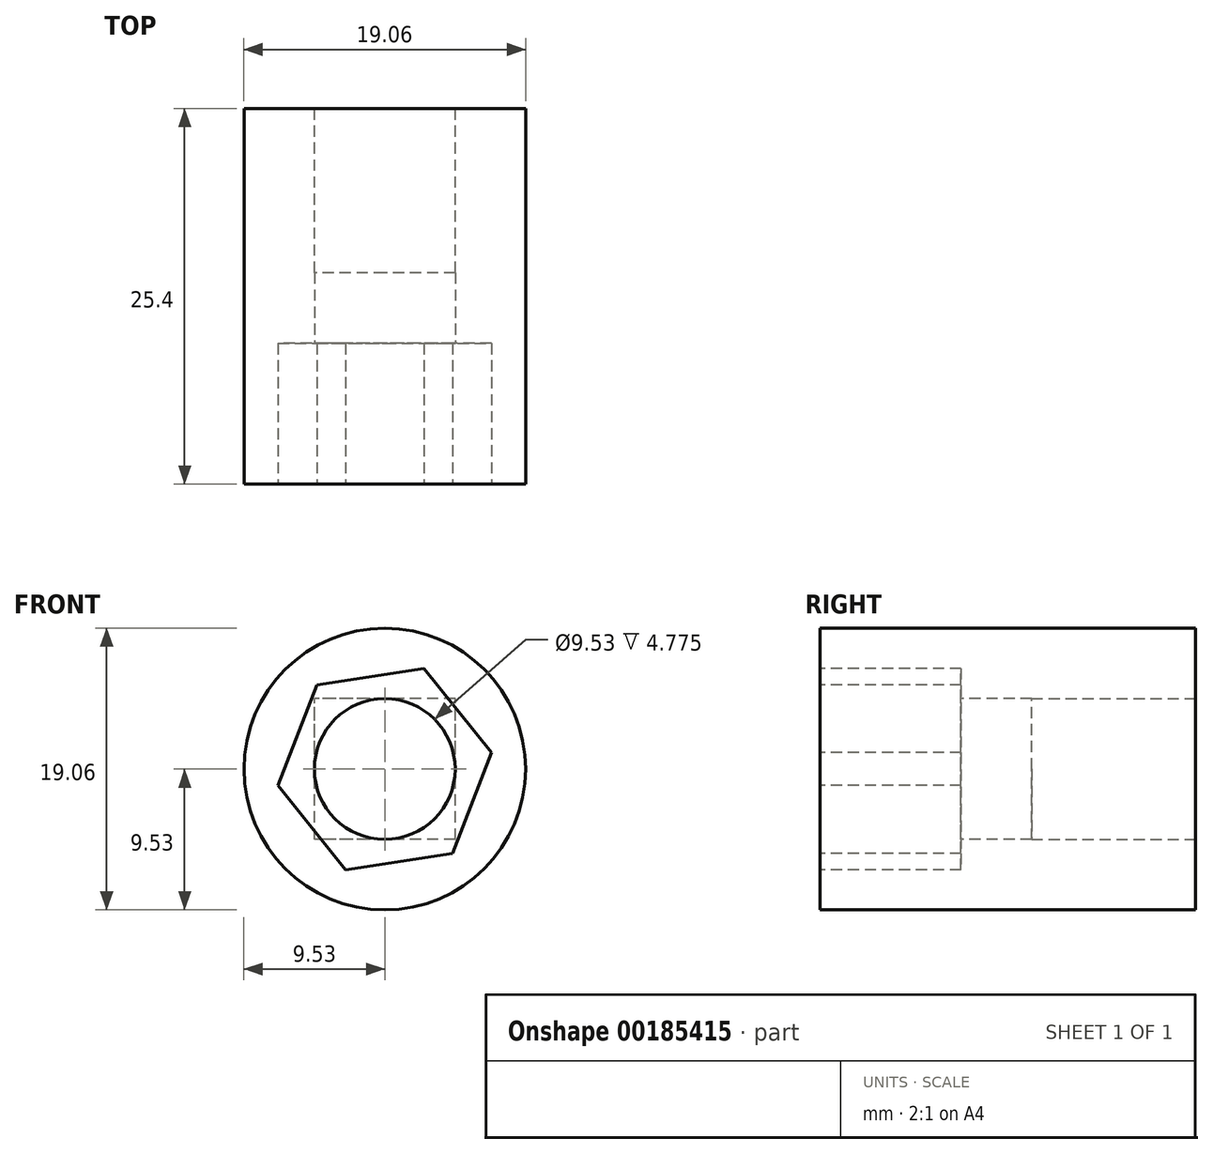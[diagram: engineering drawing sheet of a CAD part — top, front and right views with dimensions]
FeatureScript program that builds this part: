
annotation { "Feature Type Name" : "Feature", "Feature Type Description" : "" }
export const myFeature = defineFeature(function(context is Context, id is Id, definition is map)
    precondition{}
    {
        {
            var Q0;
            Q0=qCreatedBy(makeId("Front.planeOp"),FACE);
            var sketch = newSketch(context, id + "F0", { "sketchPlane" : qUnion([Q0])});
            skCircle(sketch, "E0", {"center": v(0, 0) * mm, "radius": 9.53 * mm});
            skSolve(sketch);
        }
        {
            var Q0;
            Q0 = qSketchRegion(id + "F0", true);
            extrude(context, id + "F1", {"entities" : qUnion([Q0]), "depth" : 25.4 * mm});
        }
        {
            var Q0;
            Q0=qCreatedBy(makeId("Front.planeOp"),FACE);
            var sketch = newSketch(context, id + "F2", { "sketchPlane" : qUnion([Q0])});
            skLineSegment(sketch, "E1.bottom", {"start": v(4.76, -4.76) * mm, "end": v(-4.76, -4.76) * mm});
            skLineSegment(sketch, "E1.top", {"start": v(4.76, 4.76) * mm, "end": v(-4.76, 4.76) * mm});
            skLineSegment(sketch, "E1.left", {"start": v(4.76, -4.76) * mm, "end": v(4.76, 4.76) * mm});
            skLineSegment(sketch, "E1.right", {"start": v(-4.76, -4.76) * mm, "end": v(-4.76, 4.76) * mm});
            skPoint(sketch, "E1.middle", {"position": v(0, 0) * mm});
            skCircle(sketch, "E2", {"center": v(0, 0) * mm, "radius": 4.76 * mm});
            skSolve(sketch);
        }
        {
            var Q0;
            {var subQ0=sQuery(id+"F2.wireOp",EDGE,"E2");var subQ1=makeQuery(id+"F2.imprint","INTERSECT",VERTEX,{"derivedFrom":[sQuery(id+"F2.wireOp",EDGE,"E1.top"),subQ0]});Q0=makeQuery(id+"F2.imprint","IMPRINT",FACE,{"disambiguationData":[TD([[makeQuery(id+"F2.imprint","IMPRINT",EDGE,{"disambiguationData":[TD([[subQ1,1.0]])],"derivedFrom":subQ0}),1.0]])]});}
            extrude(context, id + "F3", {"entities" : qUnion([Q0]), "operationType" : NewBodyOperationType.REMOVE, "oppositeDirection" : true, "depth" : 50.8 * mm, "hasSecondDirection" : true, "secondDirectionOppositeDirection" : false, "secondDirectionDepth" : 25.4 * mm});
        }
        {
            var Q0;
            Q0 = qSketchRegion(id + "F2", true);
            extrude(context, id + "F4", {"entities" : qUnion([Q0]), "operationType" : NewBodyOperationType.REMOVE, "oppositeDirection" : true, "depth" : 11.1 * mm});
        }
        {
            var Q0;
            Q0 = qSketchRegion(id + "F2", true);
            extrude(context, id + "F5", {"entities" : qUnion([Q0]), "operationType" : NewBodyOperationType.REMOVE, "depth" : 11.1 * mm});
        }
        {
            var Q0;
            Q0=makeQuery(id+"F1.opExtrude","CAP_FACE",FACE,{"disambiguationData":[OSD([sQuery(id+"F0.wireOp",EDGE,"E0")])],"isStart":false});
            var sketch = newSketch(context, id + "F6", { "sketchPlane" : qUnion([Q0])});
            skCircle(sketch, "E3.cCircle", {"center": v(0, 0) * mm, "radius": 6.32 * mm, "construction": true});
            skLineSegment(sketch, "E3.0", {"start": v(2.64, 6.8) * mm, "end": v(7.22, 1.11) * mm});
            skLineSegment(sketch, "E3.1", {"start": v(7.22, 1.11) * mm, "end": v(4.57, -5.7) * mm});
            skLineSegment(sketch, "E3.2", {"start": v(4.57, -5.7) * mm, "end": v(-2.64, -6.8) * mm});
            skLineSegment(sketch, "E3.3", {"start": v(-2.64, -6.8) * mm, "end": v(-7.22, -1.11) * mm});
            skLineSegment(sketch, "E3.4", {"start": v(-7.22, -1.11) * mm, "end": v(-4.57, 5.7) * mm});
            skLineSegment(sketch, "E3.5", {"start": v(-4.57, 5.7) * mm, "end": v(2.64, 6.8) * mm});
            skPoint(sketch, "E3.0.midPoint", {"position": v(4.93, 3.96) * mm});
            skSolve(sketch);
        }
        {
            var Q0;
            Q0 = qSketchRegion(id + "F6", true);
            extrude(context, id + "F7", {"entities" : qUnion([Q0]), "operationType" : NewBodyOperationType.REMOVE, "oppositeDirection" : true, "depth" : 9.52 * mm});
        }
    });
